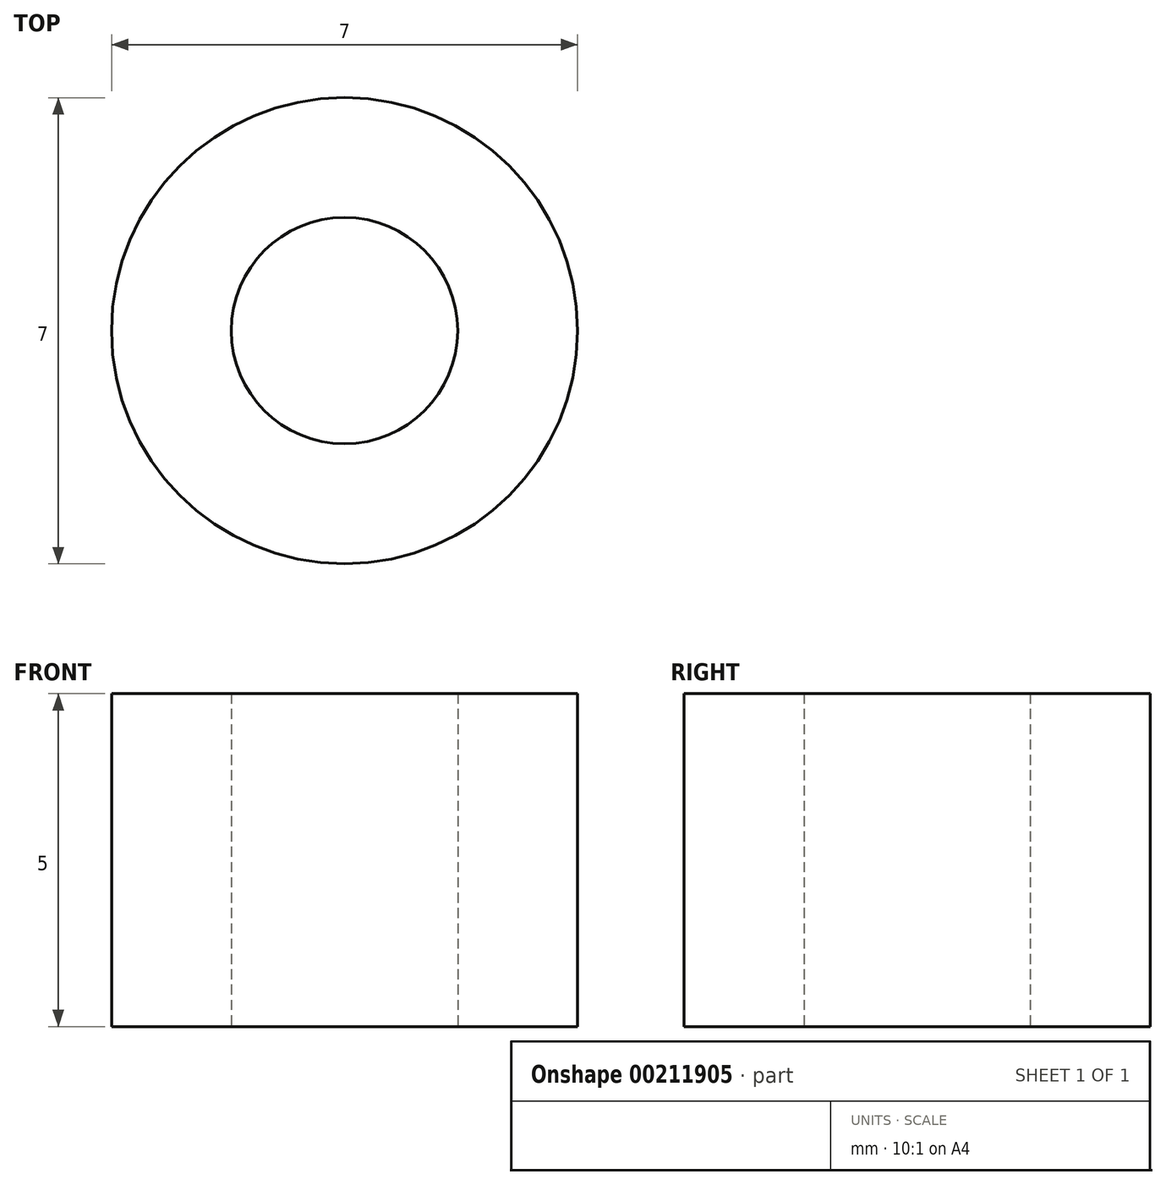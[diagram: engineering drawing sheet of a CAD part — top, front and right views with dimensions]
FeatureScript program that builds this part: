
annotation { "Feature Type Name" : "Feature", "Feature Type Description" : "" }
export const myFeature = defineFeature(function(context is Context, id is Id, definition is map)
    precondition{}
    {
        {
            var Q0;
            Q0=qCreatedBy(makeId("Top.planeOp"),FACE);
            var sketch = newSketch(context, id + "F0", { "sketchPlane" : qUnion([Q0])});
            skCircle(sketch, "E0", {"center": v(0, 3.86) * mm, "radius": 1.7 * mm});
            skCircle(sketch, "E1", {"center": v(0, 3.86) * mm, "radius": 3.5 * mm});
            skSolve(sketch);
        }
        {
            var Q0;
            Q0=makeQuery(id+"F0.imprint","IMPRINT",FACE,{"disambiguationData":[TD([[makeQuery(id+"F0.imprint","IMPRINT",EDGE,{"derivedFrom":sQuery(id+"F0.wireOp",EDGE,"E0")}),-1.0]])]});
            extrude(context, id + "F1", {"entities" : qUnion([Q0]), "depth" : 5 * mm});
        }
    });
